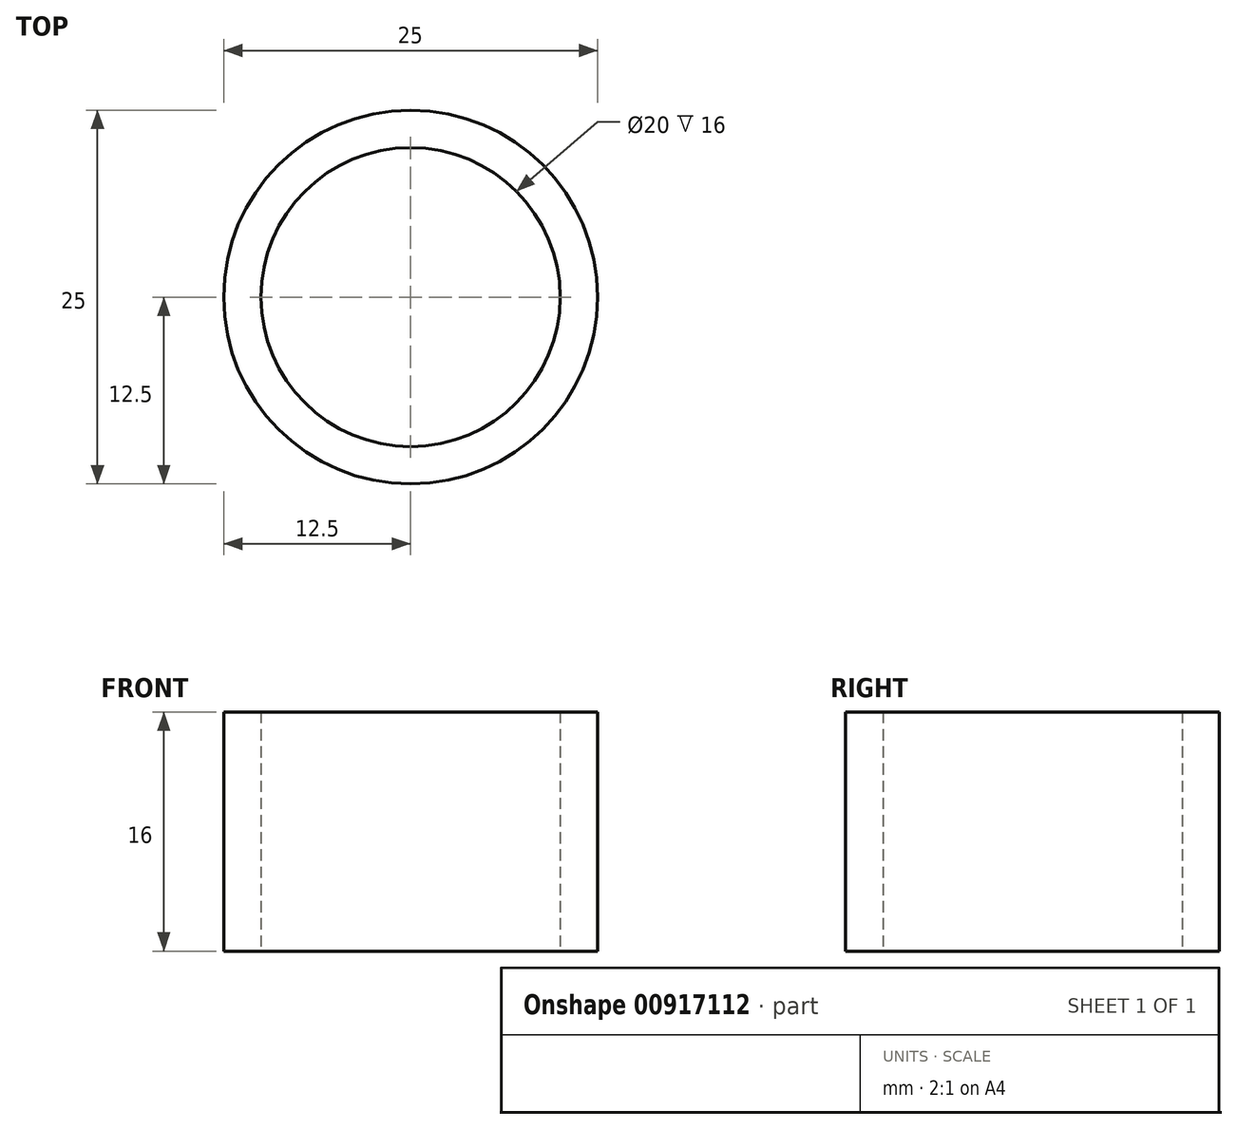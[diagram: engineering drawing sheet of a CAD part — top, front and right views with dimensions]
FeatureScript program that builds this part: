
annotation { "Feature Type Name" : "Feature", "Feature Type Description" : "" }
export const myFeature = defineFeature(function(context is Context, id is Id, definition is map)
    precondition{}
    {
        {
            var Q0;
            Q0=qCreatedBy(makeId("Top.planeOp"),FACE);
            var sketch = newSketch(context, id + "F0", { "sketchPlane" : qUnion([Q0])});
            skCircle(sketch, "E0", {"center": v(0, 0) * mm, "radius": 12.5 * mm});
            skCircle(sketch, "E1", {"center": v(0, 0) * mm, "radius": 10 * mm});
            skSolve(sketch);
        }
        {
            var Q0;
            Q0=makeQuery(id+"F0.imprint","IMPRINT",FACE,{"disambiguationData":[TD([[makeQuery(id+"F0.imprint","IMPRINT",EDGE,{"derivedFrom":sQuery(id+"F0.wireOp",EDGE,"E0")}),1.0]])]});
            extrude(context, id + "F1", {"entities" : qUnion([Q0]), "depth" : 16 * mm, "offsetDistance" : 25 * mm});
        }
    });
